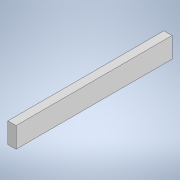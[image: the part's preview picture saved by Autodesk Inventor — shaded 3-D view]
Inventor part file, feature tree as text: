
AUTODESK INVENTOR PART (.ipt)
format: ipt  version: 2020 (Build 240168000, 168)  size: 91,648 bytes
history: native  units: mm
features: extrude x1, sketch x1
ambient origin geometry x8: Origin, YZ Plane, XZ Plane, XY Plane, X Axis, Y Axis, Z Axis, Center Point
bodies: Solide1 (feature_tree)
feature tree (2):
  extrude  "Extrusion1"  Depth=22.0mm
  sketch  "Esquisse1"
